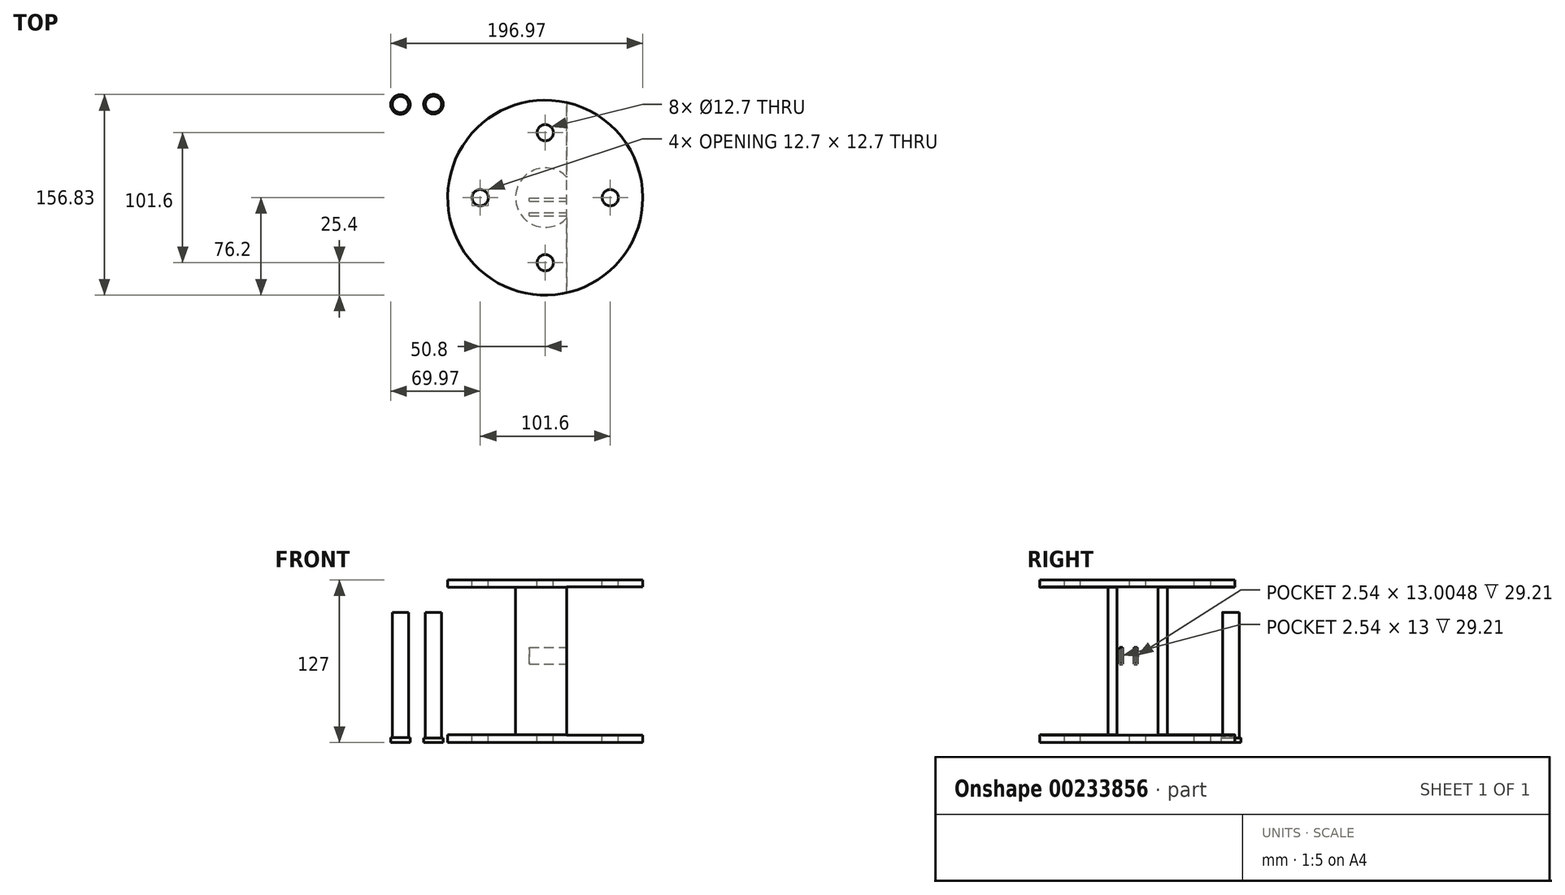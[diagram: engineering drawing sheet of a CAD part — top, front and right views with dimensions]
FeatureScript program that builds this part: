
annotation { "Feature Type Name" : "Feature", "Feature Type Description" : "" }
export const myFeature = defineFeature(function(context is Context, id is Id, definition is map)
    precondition{}
    {
        {
            var Q0;
            Q0=qCreatedBy(makeId("Top.planeOp"),FACE);
            var sketch = newSketch(context, id + "F0", { "sketchPlane" : qUnion([Q0])});
            skCircle(sketch, "E0", {"center": v(0, 0) * mm, "radius": 76.2 * mm});
            skSolve(sketch);
        }
        {
            var Q0;
            Q0=makeQuery(id+"F0.imprint","IMPRINT",FACE,{"disambiguationData":[TD([[makeQuery(id+"F0.imprint","IMPRINT",EDGE,{"derivedFrom":sQuery(id+"F0.wireOp",EDGE,"E0")}),1.0]])]});
            extrude(context, id + "F1", {"entities" : qUnion([Q0]), "depth" : 127 * mm});
        }
        {
            var Q0;
            Q0=qCreatedBy(makeId("Front.planeOp"),FACE);
            var sketch = newSketch(context, id + "F2", { "sketchPlane" : qUnion([Q0])});
            skLineSegment(sketch, "E1.bottom", {"start": v(99.32, 121.1) * mm, "end": v(23.18, 121.1) * mm});
            skLineSegment(sketch, "E1.top", {"start": v(99.32, 5.9) * mm, "end": v(23.18, 5.9) * mm});
            skLineSegment(sketch, "E1.left", {"start": v(99.32, 121.1) * mm, "end": v(99.32, 5.9) * mm});
            skLineSegment(sketch, "E1.right", {"start": v(23.18, 121.1) * mm, "end": v(23.18, 5.9) * mm});
            skLineSegment(sketch, "E2", {"start": v(0, -67.98) * mm, "end": v(0, 74.1) * mm, "construction": true});
            skLineSegment(sketch, "E3", {"start": v(0, 74.1) * mm, "end": v(0, 130.56) * mm, "construction": true});
            skLineSegment(sketch, "E4", {"start": v(0, 0) * mm, "end": v(0, 5.9) * mm});
            skLineSegment(sketch, "E5", {"start": v(0, 5.9) * mm, "end": v(11.9, 5.9) * mm, "construction": true});
            skLineSegment(sketch, "E6", {"start": v(11.9, 5.9) * mm, "end": v(23.18, 5.9) * mm, "construction": true});
            skLineSegment(sketch, "E7", {"start": v(0, 63.5) * mm, "end": v(0, 63.46) * mm});
            skLineSegment(sketch, "E8", {"start": v(0, 0) * mm, "end": v(0, 63.5) * mm, "construction": true});
            skLineSegment(sketch, "E9", {"start": v(0, 63.5) * mm, "end": v(-13.81, 63.5) * mm, "construction": true});
            skLineSegment(sketch, "E10.MirrorCS", {"start": v(0, 121.1) * mm, "end": v(11.9, 121.1) * mm, "construction": true});
            skLineSegment(sketch, "E11.MirrorCS", {"start": v(11.9, 121.1) * mm, "end": v(23.18, 121.1) * mm, "construction": true});
            skSolve(sketch);
        }
        {
            var Q0;
            Q0 = qSketchRegion(id + "F2", true);
            var Q1;
            Q1=sQuery(id+"F2.wireOp",EDGE,"E2");
            revolve(context, id + "F3", {"operationType" : NewBodyOperationType.REMOVE, "entities" : qUnion([Q0]), "axis" : qUnion([Q1]), "revolveType" : RevolveType.FULL, "oppositeDirection" : true});
        }
        {
            var Q0;
            Q0=makeQuery(id+"F1.opExtrude","CAP_FACE",FACE,{"disambiguationData":[OSD([sQuery(id+"F0.wireOp",EDGE,"E0")])],"isStart":false});
            var sketch = newSketch(context, id + "F4", { "sketchPlane" : qUnion([Q0])});
            skLineSegment(sketch, "E12", {"start": v(0, 0) * mm, "end": v(50.8, 0) * mm, "construction": true});
            skLineSegment(sketch, "E13", {"start": v(0, 0) * mm, "end": v(0, 50.8) * mm, "construction": true});
            skLineSegment(sketch, "E14.MirrorCS", {"start": v(0, 0) * mm, "end": v(-50.8, 0) * mm, "construction": true});
            skLineSegment(sketch, "E15.MirrorCS", {"start": v(0, 0) * mm, "end": v(0, -50.8) * mm, "construction": true});
            skCircle(sketch, "E16", {"center": v(0, 50.8) * mm, "radius": 6.35 * mm});
            skCircle(sketch, "E17", {"center": v(50.8, 0) * mm, "radius": 6.35 * mm});
            skCircle(sketch, "E18", {"center": v(-50.8, 0) * mm, "radius": 6.35 * mm});
            skCircle(sketch, "E19", {"center": v(0, -50.8) * mm, "radius": 6.35 * mm});
            skSolve(sketch);
        }
        {
            var Q0;
            Q0 = qSketchRegion(id + "F4", true);
            extrude(context, id + "F5", {"entities" : qUnion([Q0]), "operationType" : NewBodyOperationType.REMOVE, "oppositeDirection" : true, "depth" : 136.9 * mm});
        }
        {
            var Q0;
            Q0=qCreatedBy(makeId("Top.planeOp"),FACE);
            var sketch = newSketch(context, id + "F6", { "sketchPlane" : qUnion([Q0])});
            skCircle(sketch, "E20", {"center": v(-113.15, 72.75) * mm, "radius": 7.62 * mm});
            skCircle(sketch, "E21", {"center": v(-113.15, 72.75) * mm, "radius": 6.35 * mm});
            skSolve(sketch);
        }
        {
            var Q0;
            Q0 = qSketchRegion(id + "F6", true);
            extrude(context, id + "F7", {"entities" : qUnion([Q0]), "depth" : 3.8 * mm});
        }
        {
            var Q0;
            Q0=makeQuery(id+"F6.imprint","IMPRINT",FACE,{"disambiguationData":[TD([[makeQuery(id+"F6.imprint","IMPRINT",EDGE,{"derivedFrom":sQuery(id+"F6.wireOp",EDGE,"E21")}),1.0]])]});
            extrude(context, id + "F8", {"entities" : qUnion([Q0]), "operationType" : NewBodyOperationType.ADD, "depth" : 101.6 * mm});
        }
        {
            var Q0;
            Q0=qCreatedBy(makeId("Top.planeOp"),FACE);
            var sketch = newSketch(context, id + "F9", { "sketchPlane" : qUnion([Q0])});
            skCircle(sketch, "E22", {"center": v(-87.32, 73.01) * mm, "radius": 7.62 * mm});
            skCircle(sketch, "E23", {"center": v(-87.32, 73.01) * mm, "radius": 6.35 * mm});
            skSolve(sketch);
        }
        {
            var Q0;
            Q0 = qSketchRegion(id + "F9", true);
            extrude(context, id + "F10", {"entities" : qUnion([Q0]), "depth" : 3.56 * mm});
        }
        {
            var Q0;
            Q0=makeQuery(id+"F9.imprint","IMPRINT",FACE,{"disambiguationData":[TD([[makeQuery(id+"F9.imprint","IMPRINT",EDGE,{"derivedFrom":sQuery(id+"F9.wireOp",EDGE,"E23")}),1.0]])]});
            extrude(context, id + "F11", {"entities" : qUnion([Q0]), "operationType" : NewBodyOperationType.ADD, "depth" : 101.6 * mm});
        }
        {
            var Q0;
            Q0=qCreatedBy(makeId("Front.planeOp"),FACE);
            var sketch = newSketch(context, id + "F12", { "sketchPlane" : qUnion([Q0])});
            skLineSegment(sketch, "E24.bottom", {"start": v(134, 121.53) * mm, "end": v(16.83, 121.53) * mm});
            skLineSegment(sketch, "E24.top", {"start": v(134, 5.78) * mm, "end": v(16.83, 5.78) * mm});
            skLineSegment(sketch, "E24.left", {"start": v(134, 121.53) * mm, "end": v(134, 5.78) * mm});
            skLineSegment(sketch, "E24.right", {"start": v(16.83, 121.53) * mm, "end": v(16.83, 5.78) * mm});
            skSolve(sketch);
        }
        {
            var Q0;
            Q0=makeQuery(id+"F12.imprint","IMPRINT",FACE,{"disambiguationData":[TD([[makeQuery(id+"F12.imprint","IMPRINT",EDGE,{"derivedFrom":sQuery(id+"F12.wireOp",EDGE,"E24.bottom")}),1.0]])]});
            extrude(context, id + "F13", {"entities" : qUnion([Q0]), "operationType" : NewBodyOperationType.REMOVE, "endBound" : BoundingType.SYMMETRIC, "depth" : 177.8 * mm});
        }
        {
            var Q0;
            Q0=makeQuery(id+"F13.boolean.opBoolean","COPY",FACE,{"derivedFrom":makeQuery(id+"F13.opExtrude","SWEPT_FACE",FACE,{"disambiguationData":[OSD([sQuery(id+"F12.wireOp",EDGE,"E24.right")])]})});
            var sketch = newSketch(context, id + "F14", { "sketchPlane" : qUnion([Q0])});
            skLineSegment(sketch, "E25.bottom", {"start": v(-14.23, 74.3) * mm, "end": v(-11.69, 74.3) * mm});
            skLineSegment(sketch, "E25.top", {"start": v(-14.23, 61.3) * mm, "end": v(-11.69, 61.3) * mm});
            skLineSegment(sketch, "E25.left", {"start": v(-14.23, 74.3) * mm, "end": v(-14.23, 61.3) * mm});
            skLineSegment(sketch, "E25.right", {"start": v(-11.69, 74.3) * mm, "end": v(-11.69, 61.3) * mm});
            skLineSegment(sketch, "E26", {"start": v(-11.69, 61.3) * mm, "end": v(-2.69, 61.3) * mm, "construction": true});
            skLineSegment(sketch, "E27.bottom", {"start": v(-2.69, 61.3) * mm, "end": v(-0.15, 61.3) * mm});
            skLineSegment(sketch, "E27.top", {"start": v(-2.69, 74.3) * mm, "end": v(-0.15, 74.3) * mm});
            skLineSegment(sketch, "E27.left", {"start": v(-2.69, 61.3) * mm, "end": v(-2.69, 74.3) * mm});
            skLineSegment(sketch, "E27.right", {"start": v(-0.15, 61.3) * mm, "end": v(-0.15, 74.3) * mm});
            skSolve(sketch);
        }
        {
            var Q0;
            Q0 = qSketchRegion(id + "F14", true);
            extrude(context, id + "F15", {"entities" : qUnion([Q0]), "operationType" : NewBodyOperationType.REMOVE, "oppositeDirection" : true, "depth" : 29.2 * mm});
        }
    });
